# Revit family: Шумоглушитель круглый N
name_source: partatom
category: Арматура воздуховодов
units: mm (PartAtom-declared; Revit-internal decimal feet)

## family parameters
Всегда вертикально = Нет
Заголовок OmniClass = Climate Control (HVAC)
На основе рабочей плоскости = Нет
Номер OmniClass = 23.75.00.00
Общий = Нет
При загрузке вырезать с полостями = Нет
Размер круглого соединителя = Использовать диаметр
Тип детали = Вставляется

## types (12) — shared parameters
ADSK_Единица измерения = шт.
ADSK_Завод-изготовитель = Naveka
ADSK_Наименование = Шумоглушитель для круглого сечения (компактный корпус)
ADSK_Примечание = https://progress-nw.ru
Материал = RAL 0000 Серый металл

## per-type parameters (varying)
| type | ADSK_Марка | ADSK_Масса_Текст | B | D | D+0.5 | D+4.5 | H | L | d | Высота | Длина | Длина УГО | Длина вертикаль пластины | Длина горизонт пластины | Ширина |
| N 6-100 | N 6-100 210х158 | 4.2 кг | 210 мм | 49 мм | 50 мм | 54 мм | 158 мм | 628 мм | 100 мм | 158 мм | 628 мм | 628 мм | 140 мм | 140 мм | 210 мм |
| N 6-125 | N 6-125 239х181 | 5.0 кг | 239 мм | 62 мм | 62 мм | 66 мм | 181 мм | 628 мм | 125 мм | 181 мм | 628 мм | 628 мм | 159 мм | 159 мм | 239 мм |
| N 6-160 | N 6-160 275х218 | 6.1 кг | 275 мм | 79 мм | 80 мм | 84 мм | 218 мм | 628 мм | 160 мм | 218 мм | 628 мм | 628 мм | 183 мм | 183 мм | 275 мм |
| N 6-200 | N 6-200 328х254 | 7.3 кг | 328 мм | 99 мм | 100 мм | 104 мм | 254 мм | 628 мм | 200 мм | 254 мм | 628 мм | 628 мм | 219 мм | 219 мм | 328 мм |
| N 6-250 | N 6-250 390х308 | 9.0 кг | 390 мм | 124 мм | 125 мм | 129 мм | 308 мм | 628 мм | 250 мм | 308 мм | 628 мм | 628 мм | 260 мм | 260 мм | 390 мм |
| N 6-315 | N 6-315 453х372 | 11.0 кг | 453 мм | 157 мм | 157 мм | 161 мм | 372 мм | 628 мм | 315 мм | 372 мм | 628 мм | 628 мм | 302 мм | 302 мм | 453 мм |
| N 9-100 | N 9-100 210х158 | 6.7 кг | 210 мм | 49 мм | 50 мм | 54 мм | 158 мм | 1028 мм | 100 мм | 158 мм | 1028 мм | 1028 мм | 140 мм | 140 мм | 210 мм |
| N 9-125 | N 9-125 239х181 | 7.9 кг | 239 мм | 62 мм | 62 мм | 66 мм | 181 мм | 1028 мм | 125 мм | 181 мм | 1028 мм | 1028 мм | 159 мм | 159 мм | 239 мм |
| N 9-160 | N 9-160 275х218 | 9.5 кг | 275 мм | 79 мм | 80 мм | 84 мм | 218 мм | 1028 мм | 160 мм | 218 мм | 1028 мм | 1028 мм | 183 мм | 183 мм | 275 мм |
| N 9-200 | N 9-200 328х254 | 11.4 кг | 328 мм | 99 мм | 100 мм | 104 мм | 254 мм | 1028 мм | 200 мм | 254 мм | 1028 мм | 1028 мм | 219 мм | 219 мм | 328 мм |
| N 9-250 | N 9-250 390х308 | 14.0 кг | 390 мм | 124 мм | 125 мм | 129 мм | 308 мм | 1028 мм | 250 мм | 308 мм | 1028 мм | 1028 мм | 260 мм | 260 мм | 390 мм |
| N 9-315 | N 9-315 453х372 | 17.0 кг | 453 мм | 157 мм | 157 мм | 161 мм | 372 мм | 1028 мм | 315 мм | 372 мм | 1028 мм | 1028 мм | 302 мм | 302 мм | 453 мм |
